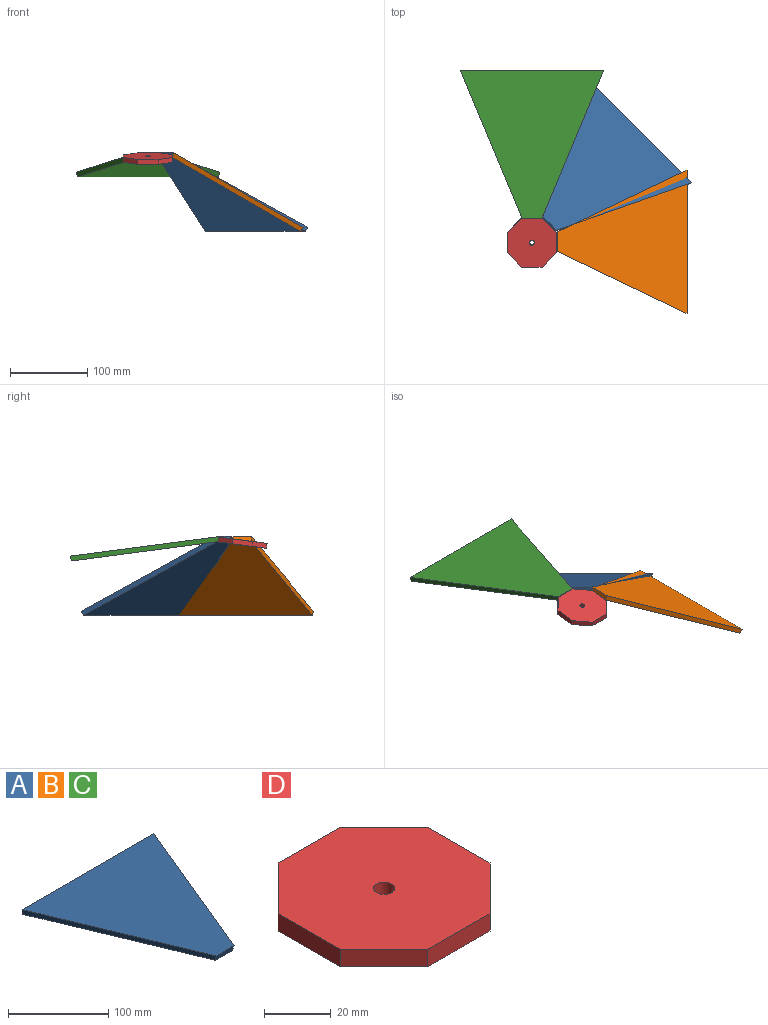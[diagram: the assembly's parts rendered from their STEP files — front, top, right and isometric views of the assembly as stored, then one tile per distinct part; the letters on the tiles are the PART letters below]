
ASSEMBLY  parts=4 mates=1
PART A: 6 faces, bbox 185.8x193.6x6.4 mm
  f0: plane 185.78x6.35mm, normal (0,1,0), area 1171mm2, adj f1,f3,f4,f5
  f1: plane 193.6x80.85mm, normal (-0.91,-0.38,-0.2), area 1350.7mm2, adj f0,f2,f4,f5
  f2: plane 25.4x6.35mm, normal (0,-0.97,-0.26), area 162.6mm2, adj f1,f3,f4,f5
  f3: plane 193.6x80.85mm, normal (0.91,-0.38,-0.2), area 1350.7mm2, adj f0,f2,f4,f5
  f4: plane 193.6x185.78mm, normal (0,0,1), area 20442.4mm2, adj f0,f1,f2,f3
  f5: plane 191.9x183.05mm, normal (0,0,-1), area 19873.2mm2, adj f0,f1,f2,f3
PART B: same geometry as A
PART C: same geometry as A
PART D: 11 faces, bbox 63.5x63.5x6.4 mm
  f0: plane 18.6x18.6mm, normal (-0.71,-0.71,0), area 167mm2, adj f1,f7,f8,f9
  f1: plane 26.3x6.35mm, normal (0,-1,0), area 167mm2, adj f0,f2,f8,f9
  f2: plane 18.6x18.6mm, normal (0.71,-0.71,0), area 167mm2, adj f1,f3,f8,f9
  f3: plane 26.3x6.35mm, normal (1,0,0), area 167mm2, adj f2,f4,f8,f9
  f4: plane 18.6x18.6mm, normal (0.71,0.71,0), area 167mm2, adj f3,f5,f8,f9
  f5: plane 26.3x6.35mm, normal (0,1,0), area 167mm2, adj f4,f6,f8,f9
  f6: plane 18.6x18.6mm, normal (-0.71,0.71,0), area 167mm2, adj f5,f7,f8,f9
  f7: plane 26.3x6.35mm, normal (-1,0,0), area 167mm2, adj f0,f6,f8,f9
  f8: plane 63.5x63.5mm, normal (0,0,1), area 3308.8mm2, adj f0,f1,f2,f3,f4,f5,f6,f7
  f9: plane 63.5x63.5mm, normal (0,0,-1), area 3308.8mm2, adj f0,f1,f2,f3,f4,f5,f6,f7
  f10: cylinder r=3.17mm len=6.35mm, axis (0,0,1), area 126.7mm2, adj f8,f9
PLACE A rot(axis=(-0.53,0.22,-0.82),53.6deg) t=(11.9,34.88,-2.63)mm
PLACE B rot(axis=(-0.25,0.25,-0.94),93.8deg) t=(30.5,17.04,-2.75)mm
PLACE C rot(axis=(-1,0,0),7.5deg) t=(-12.3,33.53,-3.61)mm
PLACE D rot(axis=(1,0,0),7.5deg) t=(0.25,3.78,-8.26)mm
MATE planar D.f5 <-> C.f2  axis (0,0.99,0.13) through (0.25,34.84,-0.97)mm
